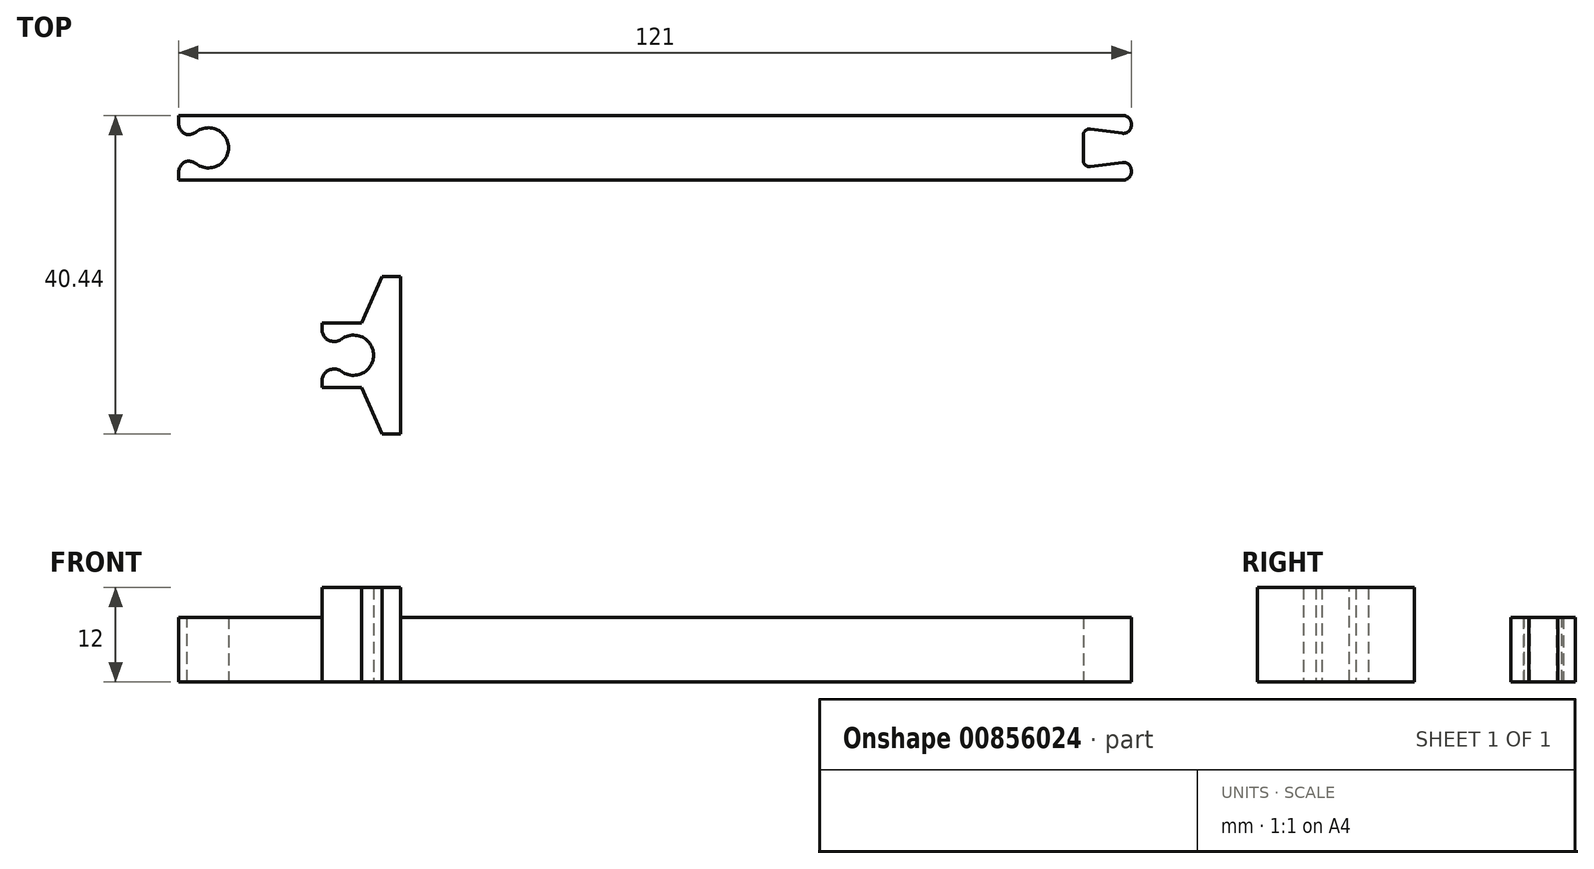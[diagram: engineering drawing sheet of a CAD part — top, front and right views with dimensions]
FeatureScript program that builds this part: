
annotation { "Feature Type Name" : "Feature", "Feature Type Description" : "" }
export const myFeature = defineFeature(function(context is Context, id is Id, definition is map)
    precondition{}
    {
        {
            var Q0;
            Q0=qCreatedBy(makeId("Top.planeOp"),FACE);
            var sketch = newSketch(context, id + "F0", { "sketchPlane" : qUnion([Q0])});
            skLineSegment(sketch, "E0.bottom", {"start": v(-50.76, -1.26) * mm, "end": v(70.24, -1.26) * mm});
            skLineSegment(sketch, "E0.top", {"start": v(-50.76, -9.46) * mm, "end": v(70.24, -9.46) * mm});
            skLineSegment(sketch, "E0.left", {"start": v(-50.76, -1.26) * mm, "end": v(-50.76, -9.46) * mm});
            skLineSegment(sketch, "E0.right", {"start": v(70.24, -1.26) * mm, "end": v(70.24, -9.46) * mm});
            skPoint(sketch, "E1.centerSnap0", {"position": v(-50.76, -5.36) * mm});
            skPoint(sketch, "E2.first.point", {"position": v(-49.56, -5.36) * mm});
            skCircle(sketch, "E3", {"center": v(-46.98, -5.36) * mm, "radius": 2.55 * mm});
            skLineSegment(sketch, "E4.right", {"start": v(-50.76, -5.3) * mm, "end": v(-50.76, -5.36) * mm});
            skLineSegment(sketch, "E5.bottom", {"start": v(-48.9, -7.03) * mm, "end": v(-52.61, -7.03) * mm});
            skLineSegment(sketch, "E5.top", {"start": v(-48.9, -3.68) * mm, "end": v(-52.61, -3.68) * mm});
            skLineSegment(sketch, "E5.left", {"start": v(-48.9, -7.03) * mm, "end": v(-48.9, -3.68) * mm});
            skLineSegment(sketch, "E6", {"start": v(70.24, -5.36) * mm, "end": v(64.14, -5.36) * mm, "construction": true});
            skLineSegment(sketch, "E7", {"start": v(64.14, -1.26) * mm, "end": v(64.14, -2.86) * mm, "construction": true});
            skLineSegment(sketch, "E8", {"start": v(64.14, -9.46) * mm, "end": v(64.14, -7.86) * mm, "construction": true});
            skLineSegment(sketch, "E9", {"start": v(64.14, -7.86) * mm, "end": v(64.14, -2.86) * mm});
            skLineSegment(sketch, "E10", {"start": v(70.24, -5.36) * mm, "end": v(70.24, -3.66) * mm, "construction": true});
            skLineSegment(sketch, "E11", {"start": v(70.24, -5.36) * mm, "end": v(70.24, -7.06) * mm, "construction": true});
            skLineSegment(sketch, "E12", {"start": v(70.24, -7.06) * mm, "end": v(64.14, -7.86) * mm});
            skLineSegment(sketch, "E13", {"start": v(64.14, -2.86) * mm, "end": v(70.24, -3.66) * mm});
            skSolve(sketch);
        }
        {
            var Q0;
            {var subQ9=sQuery(id+"F0.wireOp",EDGE,"E0.bottom");Q0=makeQuery(id+"F0.imprint","IMPRINT",FACE,{"disambiguationData":[TD([[makeQuery(id+"F0.imprint","IMPRINT",EDGE,{"derivedFrom":subQ9}),-1.0]])]});}
            extrude(context, id + "F1", {"entities" : qUnion([Q0]), "depth" : 8.2 * mm, "offsetDistance" : 25 * mm});
        }
        {
            var Q0;
            Q0=makeQuery(id+"F1.opExtrude","SWEPT_EDGE",EDGE,{"disambiguationData":[OSD([sQuery(id+"F0.wireOp",EDGE,"E3"),sQuery(id+"F0.wireOp",EDGE,"E5.bottom"),sQuery(id+"F0.wireOp",EDGE,"E5.left")])]});
            fillet(context, id + "F2", {"entities" : qUnion([Q0]), "radius" : 2 * mm, "tangentPropagation" : true, "allowEdgeOverflow" : false});
        }
        {
            var Q0;
            Q0=makeQuery(id+"F1.opExtrude","SWEPT_EDGE",EDGE,{"disambiguationData":[OSD([sQuery(id+"F0.wireOp",EDGE,"E0.left"),sQuery(id+"F0.wireOp",EDGE,"E5.bottom")])]});
            fillet(context, id + "F3", {"entities" : qUnion([Q0]), "radius" : 1.5 * mm, "tangentPropagation" : true, "allowEdgeOverflow" : false});
        }
        {
            var Q0;
            Q0=makeQuery(id+"F1.opExtrude","SWEPT_EDGE",EDGE,{"disambiguationData":[OSD([sQuery(id+"F0.wireOp",EDGE,"E3"),sQuery(id+"F0.wireOp",EDGE,"E5.top"),sQuery(id+"F0.wireOp",EDGE,"E5.left")])]});
            fillet(context, id + "F4", {"entities" : qUnion([Q0]), "radius" : 2 * mm, "tangentPropagation" : true, "allowEdgeOverflow" : false});
        }
        {
            var Q0;
            Q0=makeQuery(id+"F1.opExtrude","SWEPT_EDGE",EDGE,{"disambiguationData":[OSD([sQuery(id+"F0.wireOp",EDGE,"E0.left"),sQuery(id+"F0.wireOp",EDGE,"E5.top")])]});
            fillet(context, id + "F5", {"entities" : qUnion([Q0]), "radius" : 1.5 * mm, "tangentPropagation" : true, "allowEdgeOverflow" : false});
        }
        {
            var Q0;
            Q0=makeQuery(id+"F1.opExtrude","SWEPT_EDGE",EDGE,{"disambiguationData":[OSD([sQuery(id+"F0.wireOp",EDGE,"E0.right"),sQuery(id+"F0.wireOp",EDGE,"E13")])]});
            var Q1;
            Q1=makeQuery(id+"F1.opExtrude","SWEPT_EDGE",EDGE,{"disambiguationData":[OSD([sQuery(id+"F0.wireOp",EDGE,"E0.right"),sQuery(id+"F0.wireOp",EDGE,"E12")])]});
            fillet(context, id + "F6", {"entities" : qUnion([Q0, Q1]), "radius" : 1 * mm, "tangentPropagation" : true, "allowEdgeOverflow" : false});
        }
        {
            var Q0;
            Q0=makeQuery(id+"F1.opExtrude","SWEPT_EDGE",EDGE,{"disambiguationData":[OSD([sQuery(id+"F0.wireOp",EDGE,"E0.bottom"),sQuery(id+"F0.wireOp",EDGE,"E0.right")])]});
            var Q1;
            Q1=makeQuery(id+"F1.opExtrude","SWEPT_EDGE",EDGE,{"disambiguationData":[OSD([sQuery(id+"F0.wireOp",EDGE,"E0.top"),sQuery(id+"F0.wireOp",EDGE,"E0.right")])]});
            fillet(context, id + "F7", {"entities" : qUnion([Q0, Q1]), "radius" : 1 * mm, "tangentPropagation" : true, "allowEdgeOverflow" : false});
        }
        {
            var Q0;
            Q0=makeQuery(id+"F1.opExtrude","SWEPT_EDGE",EDGE,{"disambiguationData":[OSD([sQuery(id+"F0.wireOp",EDGE,"E9"),sQuery(id+"F0.wireOp",EDGE,"E13")])]});
            fillet(context, id + "F8", {"entities" : qUnion([Q0]), "radius" : .8 * mm, "tangentPropagation" : true, "allowEdgeOverflow" : false});
        }
        {
            var Q0;
            Q0=makeQuery(id+"F1.opExtrude","SWEPT_EDGE",EDGE,{"disambiguationData":[OSD([sQuery(id+"F0.wireOp",EDGE,"E9"),sQuery(id+"F0.wireOp",EDGE,"E12")])]});
            fillet(context, id + "F9", {"entities" : qUnion([Q0]), "radius" : .8 * mm, "tangentPropagation" : true, "allowEdgeOverflow" : false});
        }
        {
            var Q0;
            Q0=qCreatedBy(makeId("Top.planeOp"),FACE);
            var sketch = newSketch(context, id + "F10", { "sketchPlane" : qUnion([Q0])});
            skLineSegment(sketch, "E14.bottom", {"start": v(-32.55, -27.6) * mm, "end": v(-22.55, -27.6) * mm});
            skLineSegment(sketch, "E14.top", {"start": v(-32.55, -35.8) * mm, "end": v(-22.55, -35.8) * mm});
            skLineSegment(sketch, "E14.left", {"start": v(-32.55, -27.6) * mm, "end": v(-32.55, -35.8) * mm});
            skLineSegment(sketch, "E14.right", {"start": v(-22.55, -27.6) * mm, "end": v(-22.55, -35.8) * mm});
            skLineSegment(sketch, "E15", {"start": v(-32.55, -31.7) * mm, "end": v(-28.55, -31.7) * mm, "construction": true});
            skLineSegment(sketch, "E16", {"start": v(-32.55, -31.7) * mm, "end": v(-32.55, -29.95) * mm, "construction": true});
            skLineSegment(sketch, "E17", {"start": v(-32.55, -31.7) * mm, "end": v(-32.55, -33.45) * mm, "construction": true});
            skCircle(sketch, "E18", {"center": v(-28.55, -31.7) * mm, "radius": 2.55 * mm});
            skLineSegment(sketch, "E19.bottom", {"start": v(-32.55, -29.95) * mm, "end": v(-30.4, -29.95) * mm});
            skLineSegment(sketch, "E19.top", {"start": v(-32.55, -33.45) * mm, "end": v(-30.4, -33.45) * mm});
            skLineSegment(sketch, "E19.left", {"start": v(-32.55, -29.95) * mm, "end": v(-32.55, -33.45) * mm});
            skLineSegment(sketch, "E19.right", {"start": v(-30.4, -29.95) * mm, "end": v(-30.4, -33.45) * mm});
            skLineSegment(sketch, "E20", {"start": v(-22.55, -31.7) * mm, "end": v(-24.95, -31.7) * mm, "construction": true});
            skLineSegment(sketch, "E21.bottom", {"start": v(-22.55, -21.7) * mm, "end": v(-24.95, -21.7) * mm});
            skLineSegment(sketch, "E21.top", {"start": v(-22.55, -41.7) * mm, "end": v(-24.95, -41.7) * mm});
            skLineSegment(sketch, "E21.left", {"start": v(-22.55, -21.7) * mm, "end": v(-22.55, -41.7) * mm});
            skLineSegment(sketch, "E21.right", {"start": v(-24.95, -21.7) * mm, "end": v(-24.95, -41.7) * mm});
            skPoint(sketch, "E21.middle", {"position": v(-23.75, -31.7) * mm});
            skLineSegment(sketch, "E22", {"start": v(-24.95, -21.7) * mm, "end": v(-27.55, -27.6) * mm});
            skLineSegment(sketch, "E23", {"start": v(-24.95, -41.7) * mm, "end": v(-27.55, -35.8) * mm});
            skSolve(sketch);
        }
        {
            var Q0;
            {var subQ12=sQuery(id+"F10.wireOp",EDGE,"E19.bottom");Q0=makeQuery(id+"F10.imprint","IMPRINT",FACE,{"disambiguationData":[TD([[makeQuery(id+"F10.imprint","IMPRINT",EDGE,{"derivedFrom":subQ12}),1.0]])]});}
            var Q1;
            {var subQ0=sQuery(id+"F10.wireOp",EDGE,"E22");Q1=makeQuery(id+"F10.imprint","IMPRINT",FACE,{"disambiguationData":[TD([[makeQuery(id+"F10.imprint","IMPRINT",EDGE,{"derivedFrom":subQ0}),1.0]])]});}
            var Q2;
            {var subQ5=sQuery(id+"F10.wireOp",EDGE,"E21.bottom");Q2=makeQuery(id+"F10.imprint","IMPRINT",FACE,{"disambiguationData":[TD([[makeQuery(id+"F10.imprint","IMPRINT",EDGE,{"derivedFrom":subQ5}),1.0]])]});}
            var Q3;
            {var subQ0=sQuery(id+"F10.wireOp",EDGE,"E21.left");var subQ1=sQuery(id+"F10.wireOp",EDGE,"E14.bottom");var subQ2=makeQuery(id+"F10.imprint","INTERSECT",VERTEX,{"derivedFrom":[subQ1,subQ0]});Q3=makeQuery(id+"F10.imprint","IMPRINT",FACE,{"disambiguationData":[TD([[makeQuery(id+"F10.imprint","IMPRINT",EDGE,{"disambiguationData":[TD([[subQ2,1.0]])],"derivedFrom":subQ1}),-1.0]])]});}
            var Q4;
            {var subQ5=sQuery(id+"F10.wireOp",EDGE,"E21.top");Q4=makeQuery(id+"F10.imprint","IMPRINT",FACE,{"disambiguationData":[TD([[makeQuery(id+"F10.imprint","IMPRINT",EDGE,{"derivedFrom":subQ5}),-1.0]])]});}
            var Q5;
            {var subQ0=sQuery(id+"F10.wireOp",EDGE,"E23");Q5=makeQuery(id+"F10.imprint","IMPRINT",FACE,{"disambiguationData":[TD([[makeQuery(id+"F10.imprint","IMPRINT",EDGE,{"derivedFrom":subQ0}),-1.0]])]});}
            extrude(context, id + "F11", {"entities" : qUnion([Q0, Q1, Q2, Q3, Q4, Q5]), "depth" : 12 * mm, "offsetDistance" : 25 * mm});
        }
        {
            var Q0;
            Q0=makeQuery(id+"F11.opExtrude","SWEPT_EDGE",EDGE,{"disambiguationData":[OSD([sQuery(id+"F10.wireOp",EDGE,"E14.left"),sQuery(id+"F10.wireOp",EDGE,"E19.top"),sQuery(id+"F10.wireOp",EDGE,"E19.left")])]});
            var Q1;
            Q1=makeQuery(id+"F11.opExtrude","SWEPT_EDGE",EDGE,{"disambiguationData":[OSD([sQuery(id+"F10.wireOp",EDGE,"E14.left"),sQuery(id+"F10.wireOp",EDGE,"E19.bottom"),sQuery(id+"F10.wireOp",EDGE,"E19.left")])]});
            fillet(context, id + "F12", {"entities" : qUnion([Q0, Q1]), "radius" : 1.5 * mm, "tangentPropagation" : true, "allowEdgeOverflow" : false});
        }
        {
            var Q0;
            Q0=makeQuery(id+"F11.opExtrude","SWEPT_EDGE",EDGE,{"disambiguationData":[OSD([sQuery(id+"F10.wireOp",EDGE,"E18"),sQuery(id+"F10.wireOp",EDGE,"E19.bottom"),sQuery(id+"F10.wireOp",EDGE,"E19.right")])]});
            var Q1;
            Q1=makeQuery(id+"F11.opExtrude","SWEPT_EDGE",EDGE,{"disambiguationData":[OSD([sQuery(id+"F10.wireOp",EDGE,"E18"),sQuery(id+"F10.wireOp",EDGE,"E19.top"),sQuery(id+"F10.wireOp",EDGE,"E19.right")])]});
            fillet(context, id + "F13", {"entities" : qUnion([Q0, Q1]), "radius" : 1.5 * mm, "tangentPropagation" : true, "allowEdgeOverflow" : false});
        }
    });
